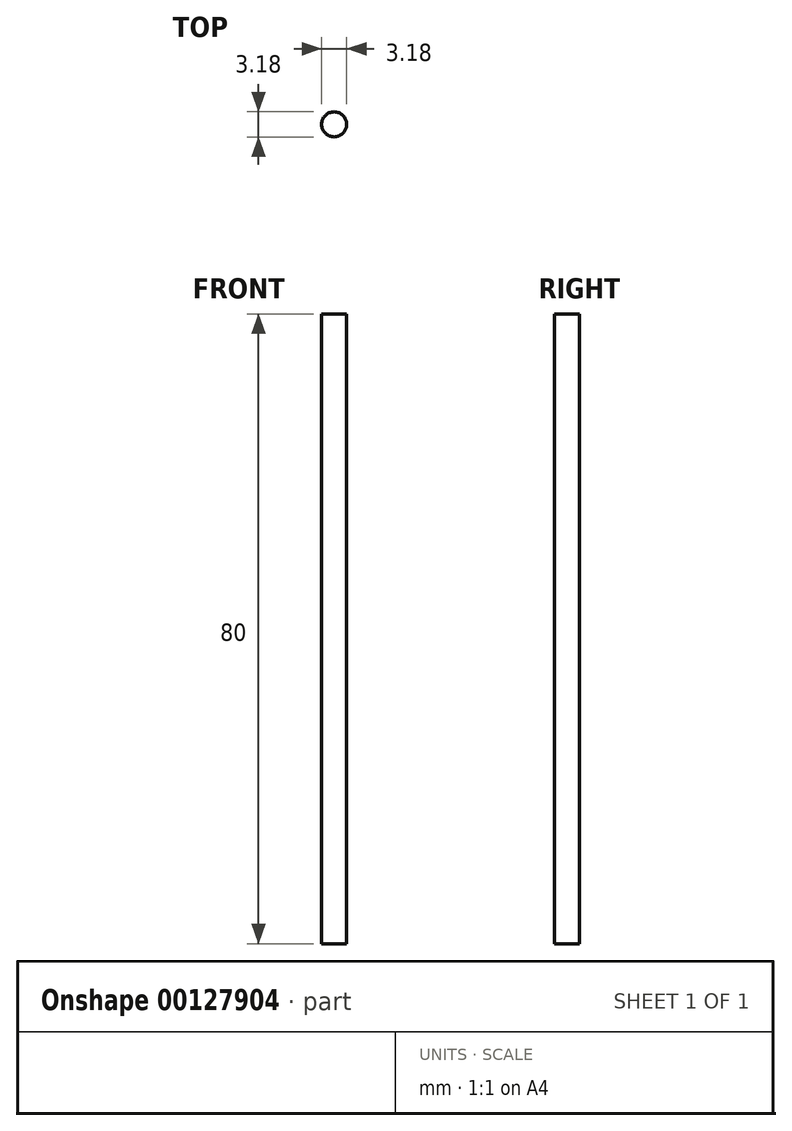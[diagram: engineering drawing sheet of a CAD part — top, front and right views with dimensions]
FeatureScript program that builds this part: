
annotation { "Feature Type Name" : "Feature", "Feature Type Description" : "" }
export const myFeature = defineFeature(function(context is Context, id is Id, definition is map)
    precondition{}
    {
        {
            var Q0;
            Q0=qCreatedBy(makeId("Top.planeOp"),FACE);
            var sketch = newSketch(context, id + "F0", { "sketchPlane" : qUnion([Q0])});
            skCircle(sketch, "E0", {"center": v(0, 0) * mm, "radius": 1.6 * mm});
            skSolve(sketch);
        }
        {
            var Q0;
            Q0=qSketchRegion(id+"F0",true);
            extrude(context, id + "F1", {"entities" : qUnion([Q0]), "depth" : 80 * mm});
        }
    });
